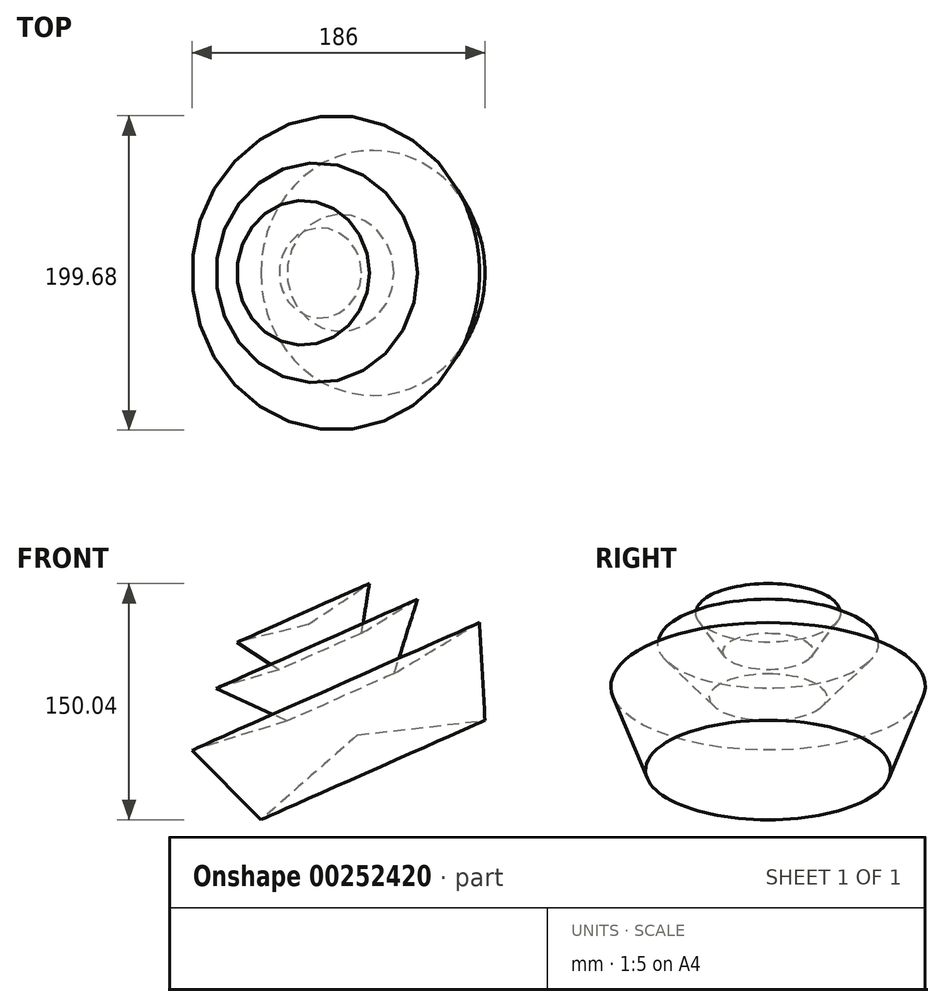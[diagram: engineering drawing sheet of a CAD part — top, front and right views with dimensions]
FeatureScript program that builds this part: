
annotation { "Feature Type Name" : "Feature", "Feature Type Description" : "" }
export const myFeature = defineFeature(function(context is Context, id is Id, definition is map)
    precondition{}
    {
        {
            var Q0;
            Q0=qCreatedBy(makeId("Front.planeOp"),FACE);
            var sketch = newSketch(context, id + "F0", { "sketchPlane" : qUnion([Q0])});
            skLineSegment(sketch, "E0", {"start": v(-47.22, 25.5) * mm, "end": v(-16.03, -44.74) * mm});
            skLineSegment(sketch, "E1", {"start": v(-16.03, -44.74) * mm, "end": v(65, -35.41) * mm});
            skLineSegment(sketch, "E2", {"start": v(65, -35.41) * mm, "end": v(61.5, 26.67) * mm});
            skLineSegment(sketch, "E3", {"start": v(61.5, 26.67) * mm, "end": v(7.29, -5.68) * mm});
            skLineSegment(sketch, "E4", {"start": v(7.29, -5.68) * mm, "end": v(22.15, 41.54) * mm});
            skLineSegment(sketch, "E5", {"start": v(-47.22, 25.5) * mm, "end": v(-8.45, 51.45) * mm});
            skLineSegment(sketch, "E6", {"start": v(-8.45, 51.45) * mm, "end": v(-13.4, 19.97) * mm});
            skLineSegment(sketch, "E7", {"start": v(-13.4, 19.97) * mm, "end": v(22.15, 41.54) * mm});
            skSolve(sketch);
        }
        {
            var Q0;
            Q0=makeQuery(id+"F0.imprint","IMPRINT",FACE,{"disambiguationData":[TD([[makeQuery(id+"F0.imprint","IMPRINT",EDGE,{"derivedFrom":sQuery(id+"F0.wireOp",EDGE,"E0")}),1.0]])]});
            var Q1;
            Q1=sQuery(id+"F0.wireOp",EDGE,"E0");
            revolve(context, id + "F1", {"entities" : qUnion([Q0]), "axis" : qUnion([Q1]), "revolveType" : RevolveType.FULL});
        }
    });
